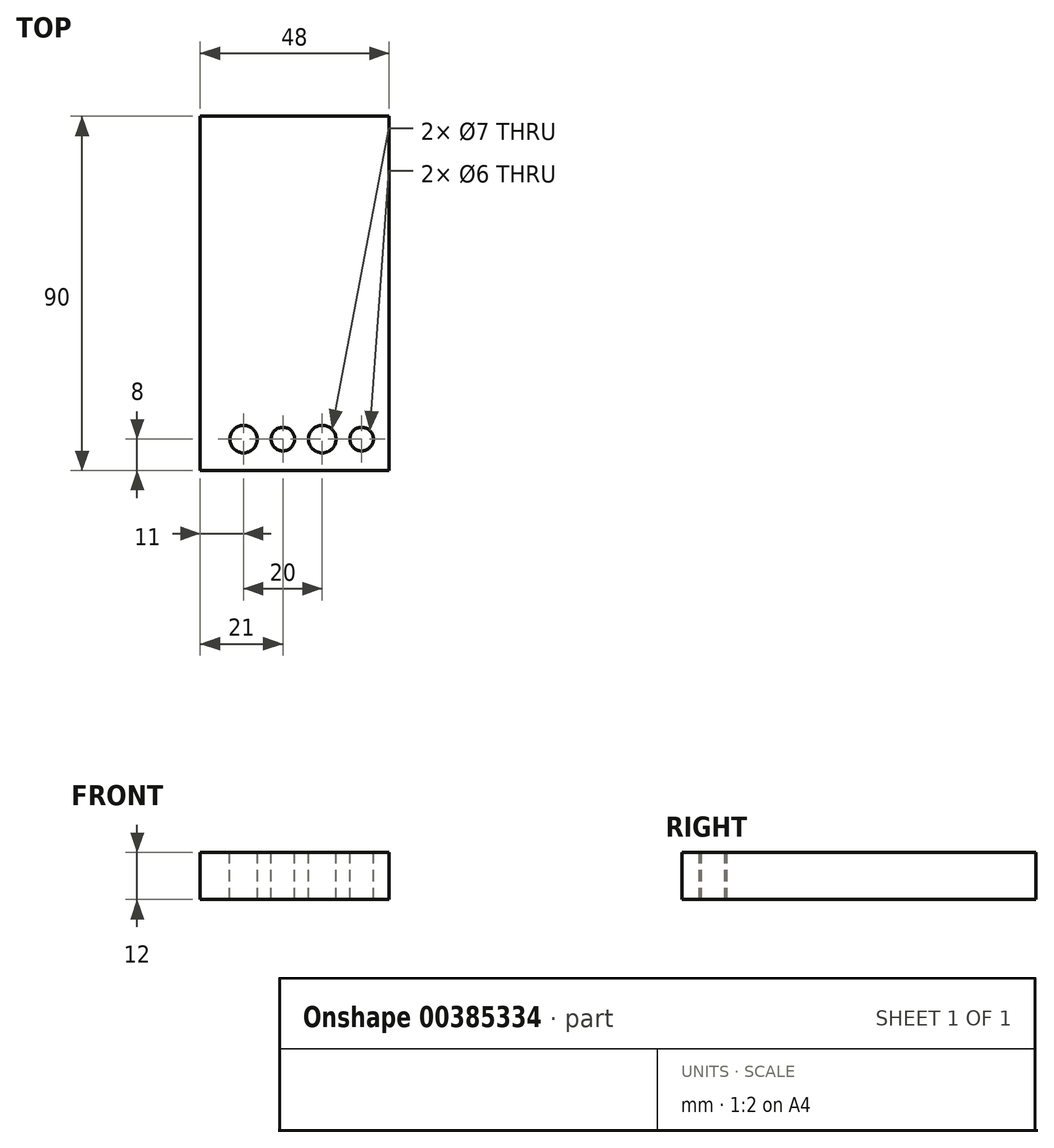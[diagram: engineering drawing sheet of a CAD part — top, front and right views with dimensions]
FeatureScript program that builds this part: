
annotation { "Feature Type Name" : "Feature", "Feature Type Description" : "" }
export const myFeature = defineFeature(function(context is Context, id is Id, definition is map)
    precondition{}
    {
        {
            var Q0;
            Q0=qCreatedBy(makeId("Top.planeOp"),FACE);
            var sketch = newSketch(context, id + "F0", { "sketchPlane" : qUnion([Q0])});
            skLineSegment(sketch, "E0.bottom", {"start": v(0, 0) * mm, "end": v(48, 0) * mm});
            skLineSegment(sketch, "E0.top", {"start": v(0, -90) * mm, "end": v(48, -90) * mm});
            skLineSegment(sketch, "E0.left", {"start": v(0, 0) * mm, "end": v(0, -90) * mm});
            skLineSegment(sketch, "E0.right", {"start": v(48, 0) * mm, "end": v(48, -90) * mm});
            skSolve(sketch);
        }
        {
            var Q0;
            Q0=makeQuery(id+"F0.imprint","IMPRINT",FACE,{"disambiguationData":[TD([[makeQuery(id+"F0.imprint","IMPRINT",EDGE,{"derivedFrom":sQuery(id+"F0.wireOp",EDGE,"E0.bottom")}),-1.0]])]});
            extrude(context, id + "F1", {"entities" : qUnion([Q0]), "depth" : 12 * mm});
        }
        {
            var Q0;
            Q0=makeQuery(id+"F1.opExtrude","CAP_FACE",FACE,{"disambiguationData":[OSD([sQuery(id+"F0.wireOp",EDGE,"E0.bottom"),sQuery(id+"F0.wireOp",EDGE,"E0.top"),sQuery(id+"F0.wireOp",EDGE,"E0.left"),sQuery(id+"F0.wireOp",EDGE,"E0.right")])],"isStart":false});
            var sketch = newSketch(context, id + "F2", { "sketchPlane" : qUnion([Q0])});
            skLineSegment(sketch, "E1", {"start": v(48, -90) * mm, "end": v(48, -82) * mm, "construction": true});
            skLineSegment(sketch, "E2", {"start": v(48, -82) * mm, "end": v(41, -82) * mm, "construction": true});
            skLineSegment(sketch, "E3", {"start": v(41, -82) * mm, "end": v(31, -82) * mm, "construction": true});
            skLineSegment(sketch, "E4", {"start": v(31, -82) * mm, "end": v(21, -82) * mm, "construction": true});
            skLineSegment(sketch, "E5", {"start": v(21, -82) * mm, "end": v(11, -82) * mm, "construction": true});
            skSolve(sketch);
        }
        {
            var Q0;
            Q0=sQuery(id+"F2.wireOp",VERTEX,"E5.end");
            var Q1;
            Q1=sQuery(id+"F2.wireOp",VERTEX,"E4.start");
            var Q2;
            Q2=makeQuery(id+"F1.opExtrude","SWEPT_BODY",BODY,{"disambiguationData":[OSD([sQuery(id+"F0.wireOp",EDGE,"E0.bottom"),sQuery(id+"F0.wireOp",EDGE,"E0.top"),sQuery(id+"F0.wireOp",EDGE,"E0.left"),sQuery(id+"F0.wireOp",EDGE,"E0.right")])]});
            hole(context, id + "F3", {"style" : HoleStyle.SIMPLE, "endStyle" : HoleEndStyle.BLIND, "holeDiameter" : 7 * mm, "holeDepth" : 12 * mm, "isTappedThrough" : true, "tappedDepth" : 12 * mm, "tapClearance" : 3, "locations" : qUnion([Q0, Q1]), "scope" : qUnion([Q2])});
        }
        {
            var Q0;
            Q0=sQuery(id+"F2.wireOp",VERTEX,"E5.start");
            var Q1;
            Q1=sQuery(id+"F2.wireOp",VERTEX,"E3.start");
            var Q2;
            Q2=makeQuery(id+"F1.opExtrude","SWEPT_BODY",BODY,{"disambiguationData":[OSD([sQuery(id+"F0.wireOp",EDGE,"E0.bottom"),sQuery(id+"F0.wireOp",EDGE,"E0.top"),sQuery(id+"F0.wireOp",EDGE,"E0.left"),sQuery(id+"F0.wireOp",EDGE,"E0.right")])]});
            hole(context, id + "F4", {"style" : HoleStyle.SIMPLE, "endStyle" : HoleEndStyle.BLIND, "holeDiameter" : 6 * mm, "holeDepth" : 12 * mm, "isTappedThrough" : true, "tappedDepth" : 12 * mm, "tapClearance" : 3, "locations" : qUnion([Q0, Q1]), "scope" : qUnion([Q2])});
        }
    });
